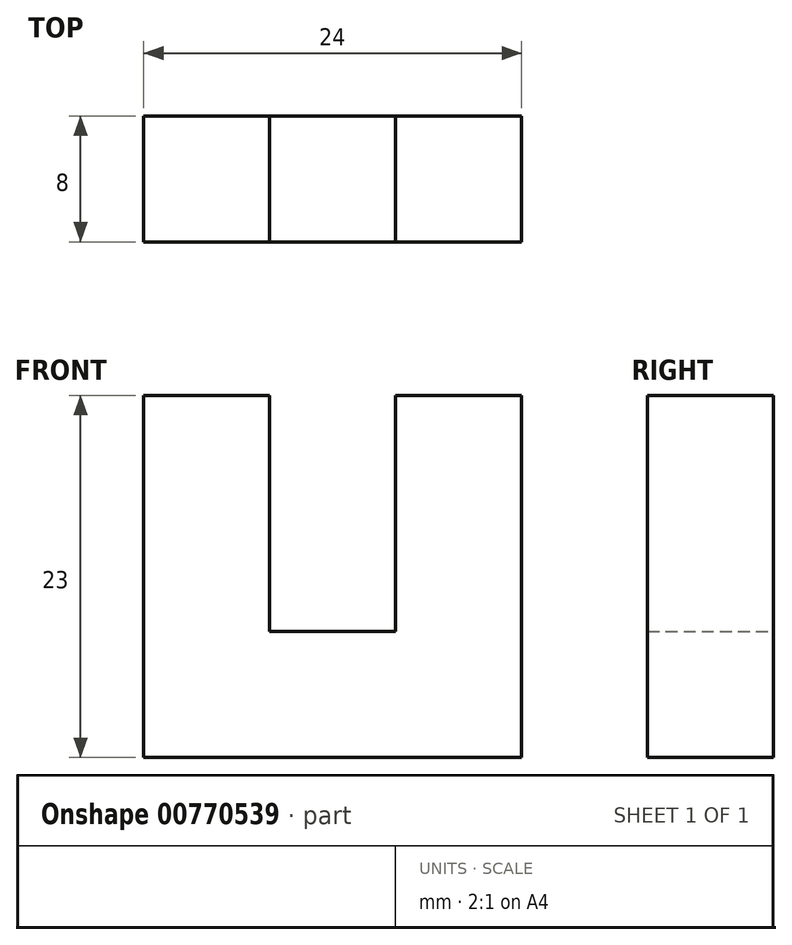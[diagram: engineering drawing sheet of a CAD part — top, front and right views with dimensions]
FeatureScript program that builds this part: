
annotation { "Feature Type Name" : "Feature", "Feature Type Description" : "" }
export const myFeature = defineFeature(function(context is Context, id is Id, definition is map)
    precondition{}
    {
        {
            var Q0;
            Q0=qCreatedBy(makeId("Front.planeOp"),FACE);
            var sketch = newSketch(context, id + "F0", { "sketchPlane" : qUnion([Q0])});
            skLineSegment(sketch, "E0", {"start": v(0, 15) * mm, "end": v(0, 0) * mm});
            skLineSegment(sketch, "E1", {"start": v(0, 0) * mm, "end": v(8, 0) * mm});
            skLineSegment(sketch, "E2", {"start": v(8, 0) * mm, "end": v(8, 15) * mm});
            skLineSegment(sketch, "E3", {"start": v(8, 15) * mm, "end": v(16, 15) * mm});
            skLineSegment(sketch, "E4", {"start": v(16, 15) * mm, "end": v(16, -8) * mm});
            skLineSegment(sketch, "E5", {"start": v(16, -8) * mm, "end": v(-8, -8) * mm});
            skLineSegment(sketch, "E6", {"start": v(-8, -8) * mm, "end": v(-8, 15) * mm});
            skLineSegment(sketch, "E7", {"start": v(-8, 15) * mm, "end": v(0, 15) * mm});
            skSolve(sketch);
        }
        {
            var Q0;
            Q0=makeQuery(id+"F0.imprint","IMPRINT",FACE,{"disambiguationData":[TD([[makeQuery(id+"F0.imprint","IMPRINT",EDGE,{"derivedFrom":sQuery(id+"F0.wireOp",EDGE,"E0")}),-1.0]])]});
            extrude(context, id + "F1", {"entities" : qUnion([Q0]), "depth" : 8 * mm, "offsetDistance" : 25 * mm});
        }
    });
